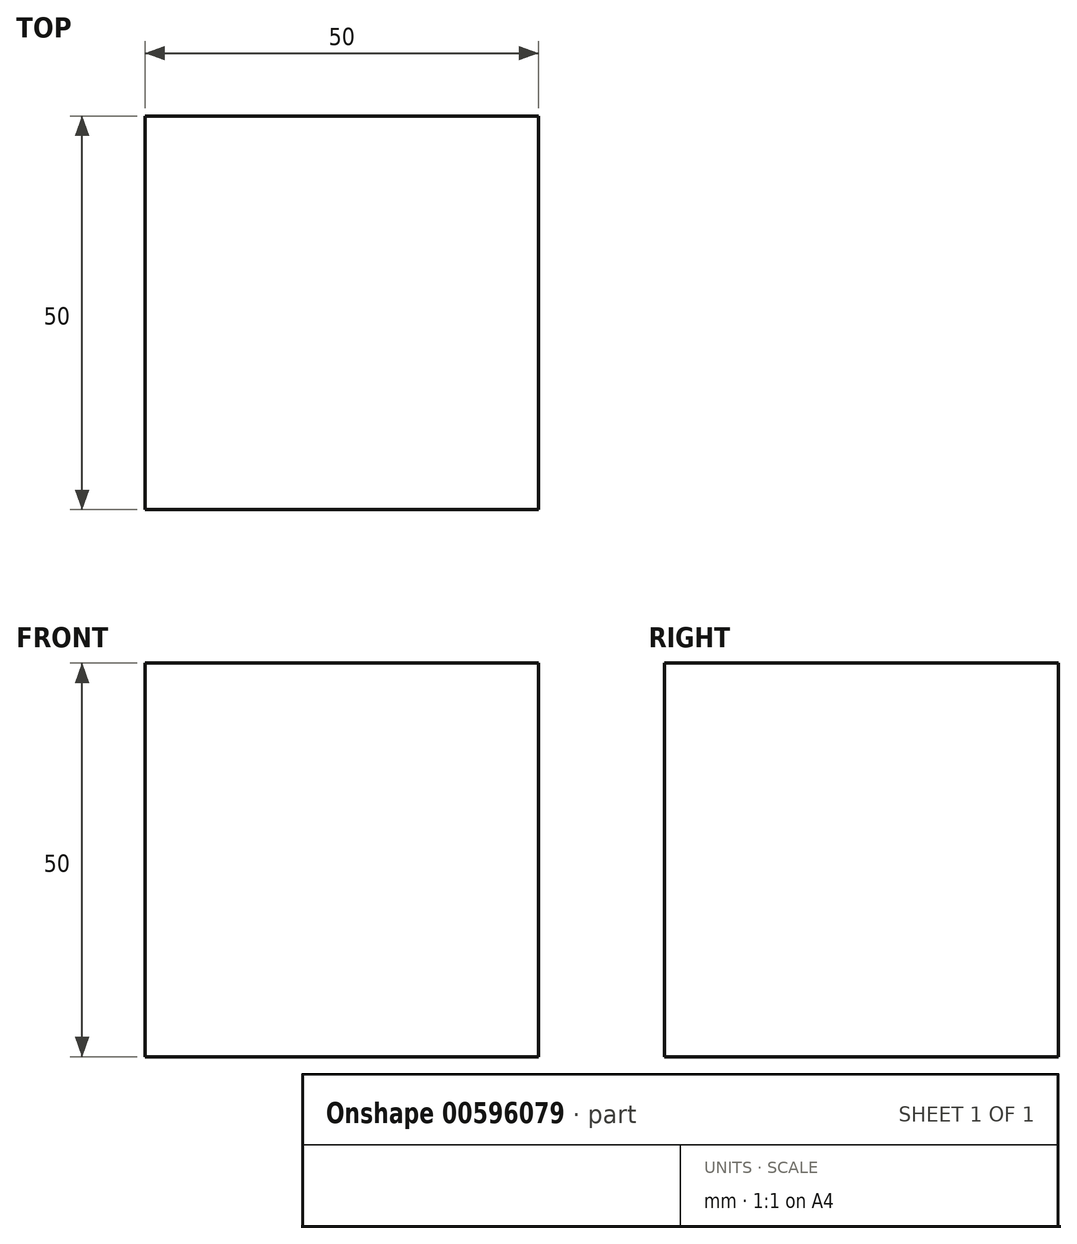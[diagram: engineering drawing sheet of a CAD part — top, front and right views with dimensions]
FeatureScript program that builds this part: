
annotation { "Feature Type Name" : "Feature", "Feature Type Description" : "" }
export const myFeature = defineFeature(function(context is Context, id is Id, definition is map)
    precondition{}
    {
        {
            var Q0;
            Q0=qCreatedBy(makeId("Top.planeOp"),FACE);
            var sketch = newSketch(context, id + "F0", { "sketchPlane" : qUnion([Q0])});
            skLineSegment(sketch, "E0.bottom", {"start": v(-25, 25) * mm, "end": v(25, 25) * mm});
            skLineSegment(sketch, "E0.top", {"start": v(-25, -25) * mm, "end": v(25, -25) * mm});
            skLineSegment(sketch, "E0.left", {"start": v(-25, 25) * mm, "end": v(-25, -25) * mm});
            skLineSegment(sketch, "E0.right", {"start": v(25, 25) * mm, "end": v(25, -25) * mm});
            skPoint(sketch, "E0.middle", {"position": v(0, 0) * mm});
            skSolve(sketch);
        }
        {
            var Q0;
            Q0=makeQuery(id+"F0.imprint","IMPRINT",FACE,{"disambiguationData":[TD([[makeQuery(id+"F0.imprint","IMPRINT",EDGE,{"derivedFrom":sQuery(id+"F0.wireOp",EDGE,"E0.bottom")}),-1.0]])]});
            extrude(context, id + "F1", {"entities" : qUnion([Q0]), "depth" : 50 * mm, "offsetDistance" : 25 * mm});
        }
    });
